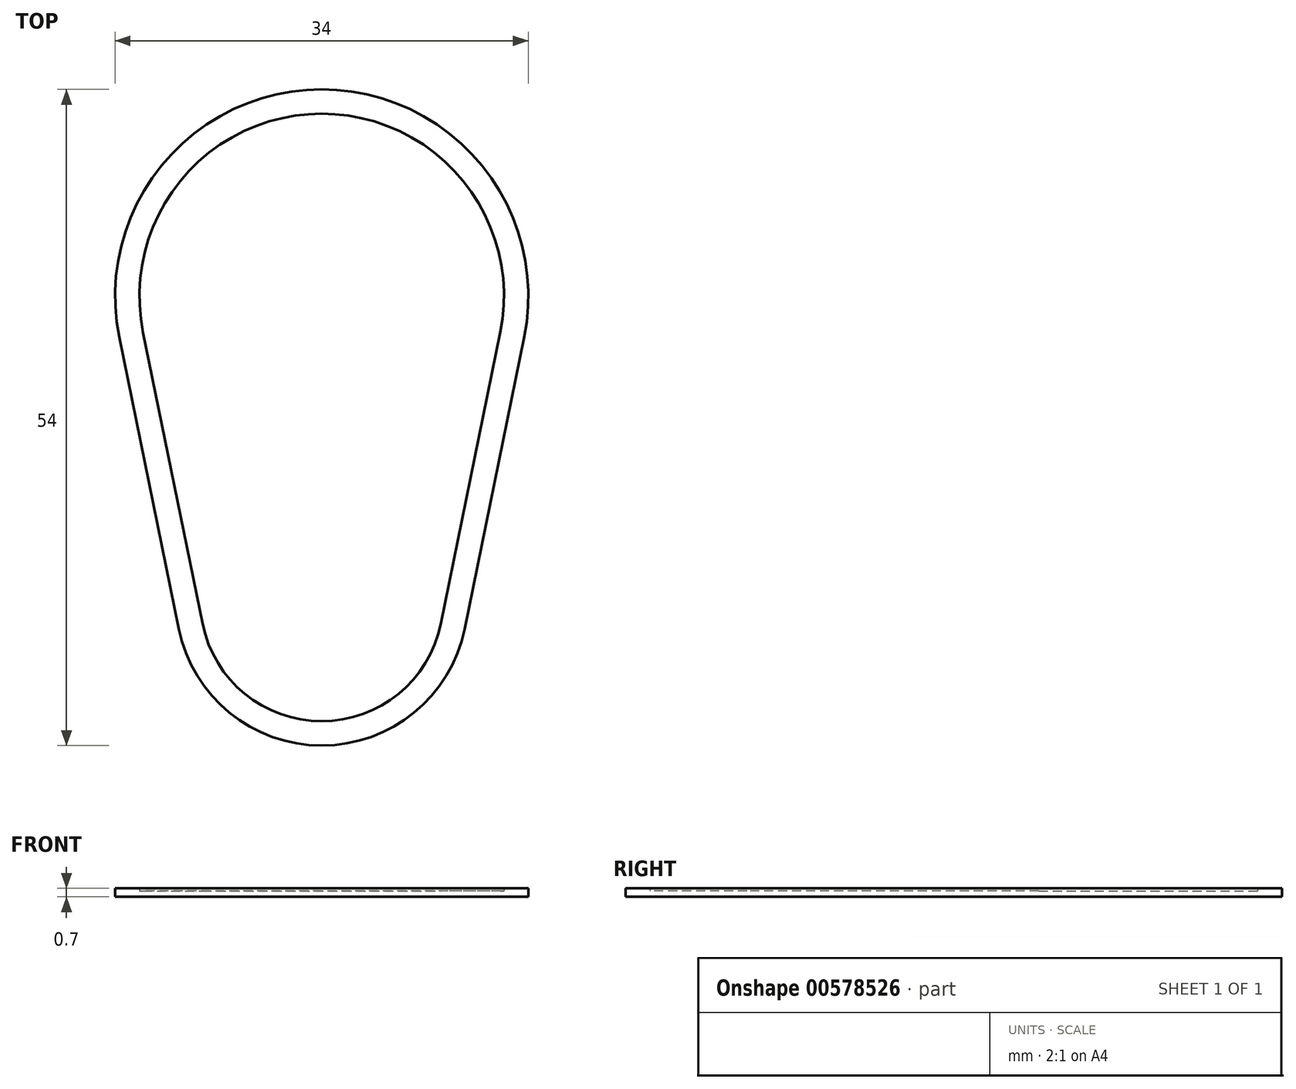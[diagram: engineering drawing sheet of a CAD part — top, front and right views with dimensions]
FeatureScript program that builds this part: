
annotation { "Feature Type Name" : "Feature", "Feature Type Description" : "" }
export const myFeature = defineFeature(function(context is Context, id is Id, definition is map)
    precondition{}
    {
        {
            var Q0;
            Q0=qCreatedBy(makeId("Top.planeOp"),FACE);
            var sketch = newSketch(context, id + "F0", { "sketchPlane" : qUnion([Q0])});
            skArc(sketch, "E0", {"start": v(14.7, 38.47) * mm, "mid": v(0, 56.47) * mm, "end": v(-14.7, 38.47) * mm});
            skArc(sketch, "E1", {"start": v(-9.8, 14.47) * mm, "mid": v(0, 6.47) * mm, "end": v(9.8, 14.47) * mm});
            skPoint(sketch, "E1.first.point", {"position": v(0, 26.47) * mm});
            skPoint(sketch, "E1.second.point", {"position": v(9.8, 14.47) * mm});
            skPoint(sketch, "E1.third.point", {"position": v(-4.66, 7.62) * mm});
            skLineSegment(sketch, "E2", {"start": v(-14.7, 38.47) * mm, "end": v(-9.8, 14.47) * mm});
            skLineSegment(sketch, "E3", {"start": v(14.7, 38.47) * mm, "end": v(9.8, 14.47) * mm});
            skLineSegment(sketch, "E4.0", {"start": v(-16.66, 38.07) * mm, "end": v(-11.76, 14.07) * mm});
            skArc(sketch, "E5.0", {"start": v(16.66, 38.07) * mm, "mid": v(0, 58.47) * mm, "end": v(-16.66, 38.07) * mm});
            skLineSegment(sketch, "E6.0", {"start": v(16.66, 38.07) * mm, "end": v(11.76, 14.07) * mm});
            skArc(sketch, "E7.0", {"start": v(-11.76, 14.07) * mm, "mid": v(0, 4.47) * mm, "end": v(11.76, 14.07) * mm});
            skSolve(sketch);
        }
        {
            var Q0;
            Q0=makeQuery(id+"F0.imprint","IMPRINT",FACE,{"disambiguationData":[TD([[makeQuery(id+"F0.imprint","IMPRINT",EDGE,{"derivedFrom":sQuery(id+"F0.wireOp",EDGE,"E0")}),1.0]])]});
            extrude(context, id + "F1", {"entities" : qUnion([Q0]), "depth" : 0.5 * mm, "offsetDistance" : 25 * mm});
        }
        {
            var Q0;
            Q0 = qSketchRegion(id + "F0", true);
            extrude(context, id + "F2", {"entities" : qUnion([Q0]), "operationType" : NewBodyOperationType.ADD, "depth" : 0.7 * mm, "offsetDistance" : 25 * mm});
        }
    });
